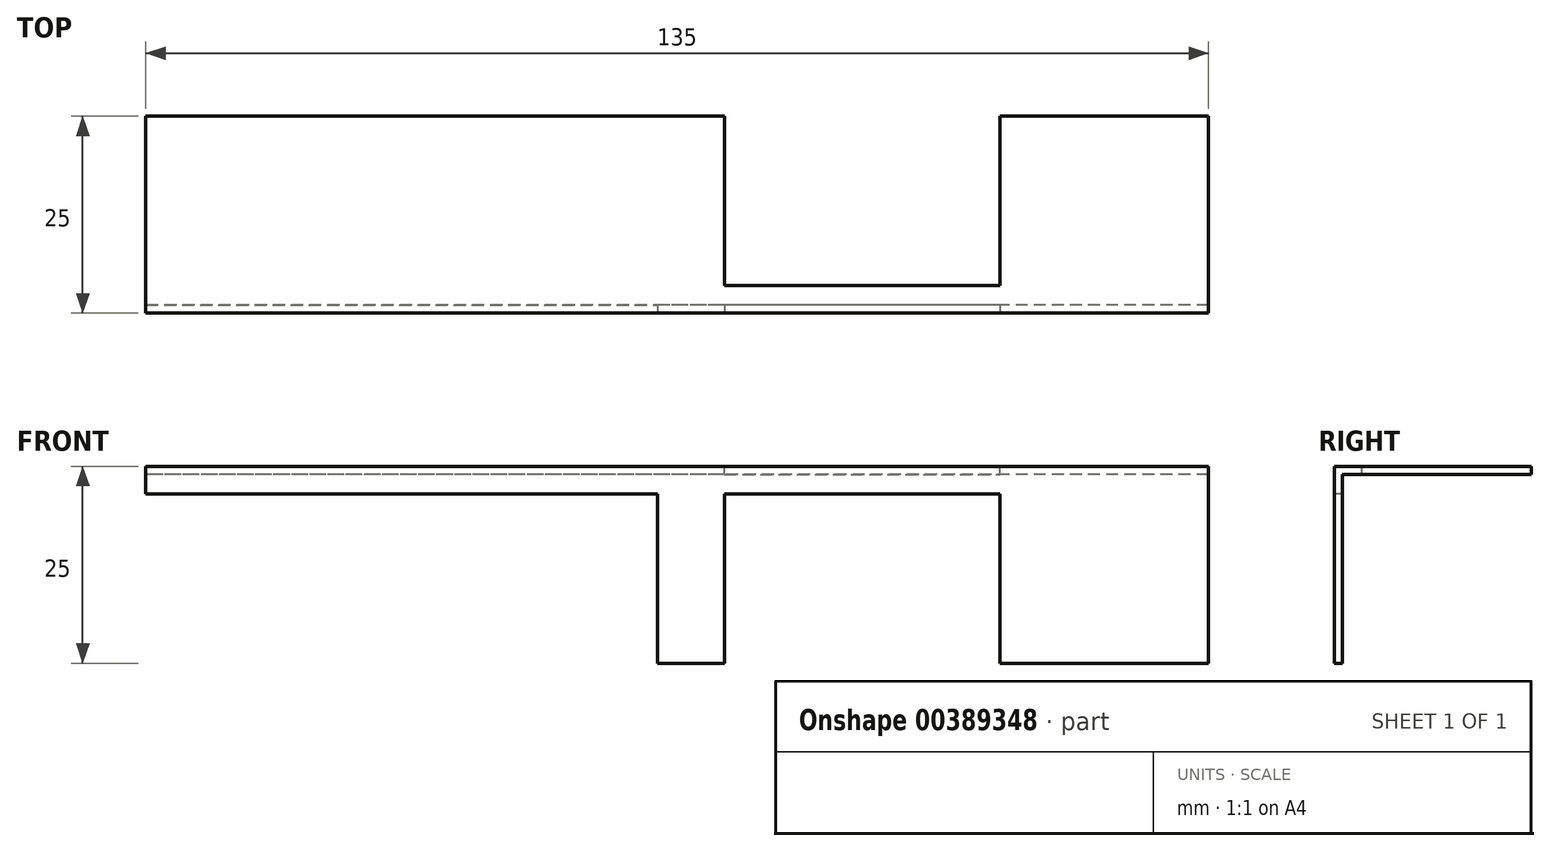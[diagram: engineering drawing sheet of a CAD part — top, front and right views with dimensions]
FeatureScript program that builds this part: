
annotation { "Feature Type Name" : "Feature", "Feature Type Description" : "" }
export const myFeature = defineFeature(function(context is Context, id is Id, definition is map)
    precondition{}
    {
        {
            var Q0;
            Q0=qCreatedBy(makeId("Right.planeOp"),FACE);
            var sketch = newSketch(context, id + "F0", { "sketchPlane" : qUnion([Q0])});
            skLineSegment(sketch, "E0.bottom", {"start": v(-65.04, 19.74) * mm, "end": v(-64.04, 19.74) * mm});
            skLineSegment(sketch, "E0.top", {"start": v(-65.04, 44.74) * mm, "end": v(-64.04, 44.74) * mm});
            skLineSegment(sketch, "E0.left", {"start": v(-65.04, 19.74) * mm, "end": v(-65.04, 44.74) * mm});
            skLineSegment(sketch, "E0.right", {"start": v(-64.04, 19.74) * mm, "end": v(-64.04, 44.74) * mm});
            skLineSegment(sketch, "E1.bottom", {"start": v(-65.04, 44.74) * mm, "end": v(-40.04, 44.74) * mm});
            skLineSegment(sketch, "E1.top", {"start": v(-65.04, 43.74) * mm, "end": v(-40.04, 43.74) * mm});
            skLineSegment(sketch, "E1.left", {"start": v(-65.04, 44.74) * mm, "end": v(-65.04, 43.74) * mm});
            skLineSegment(sketch, "E1.right", {"start": v(-40.04, 44.74) * mm, "end": v(-40.04, 43.74) * mm});
            skSolve(sketch);
        }
        {
            var Q0;
            Q0=qSketchRegion(id+"F0",true);
            extrude(context, id + "F1", {"entities" : qUnion([Q0]), "depth" : 135 * mm, "offsetDistance" : 25 * mm});
        }
        {
            var Q0;
            Q0=makeQuery(id+"F1.opExtrude","SWEPT_FACE",FACE,{"disambiguationData":[OSD([sQuery(id+"F0.wireOp",EDGE,"E1.bottom")])]});
            var sketch = newSketch(context, id + "F2", { "sketchPlane" : qUnion([Q0])});
            skLineSegment(sketch, "E2.bottom", {"start": v(73.5, -61.54) * mm, "end": v(108.5, -61.54) * mm});
            skLineSegment(sketch, "E2.top", {"start": v(73.5, -40.04) * mm, "end": v(108.5, -40.04) * mm});
            skLineSegment(sketch, "E2.left", {"start": v(73.5, -61.54) * mm, "end": v(73.5, -40.04) * mm});
            skLineSegment(sketch, "E2.right", {"start": v(108.5, -61.54) * mm, "end": v(108.5, -40.04) * mm});
            skSolve(sketch);
        }
        {
            var Q0;
            Q0=qSketchRegion(id+"F2",true);
            extrude(context, id + "F3", {"entities" : qUnion([Q0]), "operationType" : NewBodyOperationType.REMOVE, "oppositeDirection" : true, "depth" : 1 * mm, "offsetDistance" : 25 * mm});
        }
        {
            var Q0;
            Q0=makeQuery(id+"F1.opExtrude","SWEPT_FACE",FACE,{"disambiguationData":[OSD([sQuery(id+"F0.wireOp",EDGE,"E0.left"),sQuery(id+"F0.wireOp",EDGE,"E1.left")])]});
            var sketch = newSketch(context, id + "F4", { "sketchPlane" : qUnion([Q0])});
            skLineSegment(sketch, "E3.bottom", {"start": v(108.5, 19.74) * mm, "end": v(73.5, 19.74) * mm});
            skLineSegment(sketch, "E3.top", {"start": v(108.5, 41.24) * mm, "end": v(73.5, 41.24) * mm});
            skLineSegment(sketch, "E3.left", {"start": v(108.5, 19.74) * mm, "end": v(108.5, 41.24) * mm});
            skLineSegment(sketch, "E3.right", {"start": v(73.5, 19.74) * mm, "end": v(73.5, 41.24) * mm});
            skLineSegment(sketch, "E4.bottom", {"start": v(0, 19.74) * mm, "end": v(65, 19.74) * mm});
            skLineSegment(sketch, "E4.top", {"start": v(0, 41.24) * mm, "end": v(65, 41.24) * mm});
            skLineSegment(sketch, "E4.left", {"start": v(0, 19.74) * mm, "end": v(0, 41.24) * mm});
            skLineSegment(sketch, "E4.right", {"start": v(65, 19.74) * mm, "end": v(65, 41.24) * mm});
            skSolve(sketch);
        }
        {
            var Q0;
            Q0=qSketchRegion(id+"F4",true);
            extrude(context, id + "F5", {"entities" : qUnion([Q0]), "operationType" : NewBodyOperationType.REMOVE, "oppositeDirection" : true, "depth" : 1 * mm, "offsetDistance" : 25 * mm});
        }
    });
